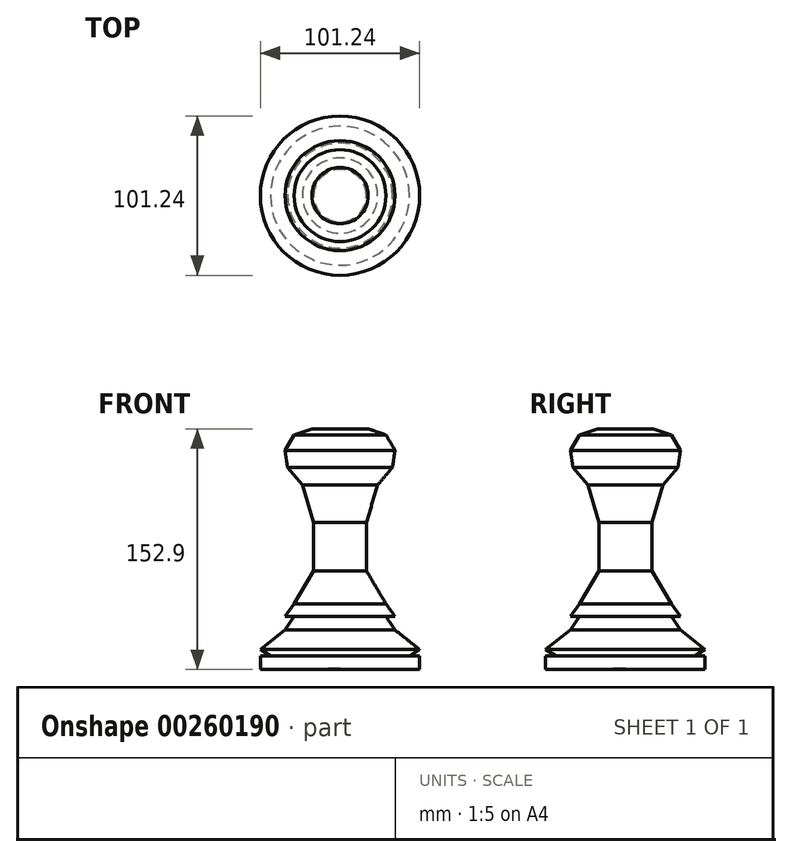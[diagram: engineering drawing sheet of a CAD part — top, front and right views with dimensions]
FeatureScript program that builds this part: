
annotation { "Feature Type Name" : "Feature", "Feature Type Description" : "" }
export const myFeature = defineFeature(function(context is Context, id is Id, definition is map)
    precondition{}
    {
        {
            var Q0;
            Q0=qCreatedBy(makeId("Front.planeOp"),FACE);
            var sketch = newSketch(context, id + "F0", { "sketchPlane" : qUnion([Q0])});
            skLineSegment(sketch, "E0", {"start": v(0, 75.87) * mm, "end": v(-17.87, 75.87) * mm});
            skLineSegment(sketch, "E1", {"start": v(-17.87, 75.87) * mm, "end": v(-29.17, 71.95) * mm});
            skLineSegment(sketch, "E2", {"start": v(-29.17, 71.95) * mm, "end": v(-34.94, 62.27) * mm});
            skLineSegment(sketch, "E3", {"start": v(-34.94, 62.27) * mm, "end": v(-33.32, 51.43) * mm});
            skLineSegment(sketch, "E4", {"start": v(-33.32, 51.43) * mm, "end": v(-23.87, 40.13) * mm});
            skLineSegment(sketch, "E5", {"start": v(-23.87, 40.13) * mm, "end": v(-16.72, 16.37) * mm});
            skLineSegment(sketch, "E6", {"start": v(-16.72, 16.37) * mm, "end": v(-16.72, -14.3) * mm});
            skLineSegment(sketch, "E7", {"start": v(-16.72, -14.3) * mm, "end": v(-29.17, -35.29) * mm});
            skLineSegment(sketch, "E8", {"start": v(-29.17, -35.29) * mm, "end": v(-34.94, -43.36) * mm});
            skLineSegment(sketch, "E9", {"start": v(-34.94, -43.36) * mm, "end": v(-29.17, -43.36) * mm});
            skLineSegment(sketch, "E10", {"start": v(-29.17, -43.36) * mm, "end": v(-34.94, -51.89) * mm});
            skPoint(sketch, "E11.end.orphan", {"position": v(0, -76.34) * mm});
            skLineSegment(sketch, "E12", {"start": v(-34.94, -51.89) * mm, "end": v(-50.62, -64.34) * mm});
            skLineSegment(sketch, "E13", {"start": v(-50.62, -64.34) * mm, "end": v(-44.16, -68.26) * mm});
            skLineSegment(sketch, "E14", {"start": v(-44.16, -68.26) * mm, "end": v(-50.62, -68.26) * mm});
            skLineSegment(sketch, "E15", {"start": v(-50.62, -68.26) * mm, "end": v(-50.62, -77.03) * mm});
            skLineSegment(sketch, "E16", {"start": v(-50.62, -77.03) * mm, "end": v(0, -76.34) * mm});
            skLineSegment(sketch, "E17", {"start": v(0, 75.87) * mm, "end": v(0, -76.34) * mm});
            skSolve(sketch);
        }
        {
            var Q0;
            Q0 = qSketchRegion(id + "F0", true);
            var Q1;
            Q1=sQuery(id+"F0.wireOp",EDGE,"E17");
            revolve(context, id + "F1", {"entities" : qUnion([Q0]), "axis" : qUnion([Q1]), "revolveType" : RevolveType.FULL});
        }
    });
